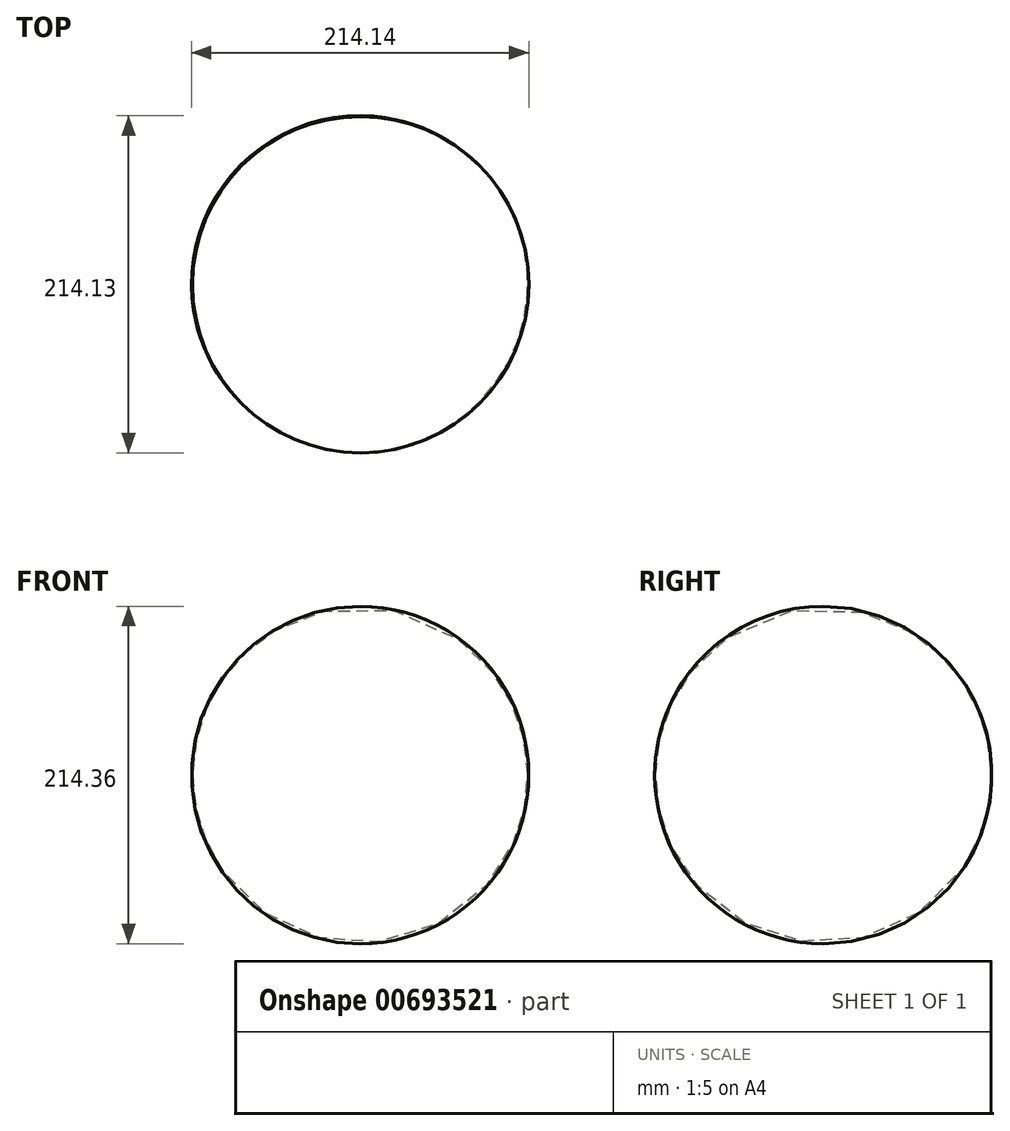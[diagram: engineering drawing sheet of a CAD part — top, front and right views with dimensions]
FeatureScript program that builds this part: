
annotation { "Feature Type Name" : "Feature", "Feature Type Description" : "" }
export const myFeature = defineFeature(function(context is Context, id is Id, definition is map)
    precondition{}
    {
        {
            var Q0;
            Q0=qCreatedBy(makeId("Top.planeOp"),FACE);
            var sketch = newSketch(context, id + "F0", { "sketchPlane" : qUnion([Q0])});
            skArc(sketch, "E0", {"start": v(76.82, 76.54) * mm, "mid": v(-74.48, 76.5) * mm, "end": v(-73.9, -74.8) * mm});
            skLineSegment(sketch, "E1", {"start": v(-73.9, -74.8) * mm, "end": v(76.82, 76.54) * mm});
            skSolve(sketch);
        }
        {
            var Q0;
            Q0=makeQuery(id+"F0.imprint","IMPRINT",FACE,{"disambiguationData":[TD([[makeQuery(id+"F0.imprint","IMPRINT",EDGE,{"derivedFrom":sQuery(id+"F0.wireOp",EDGE,"E0")}),1.0]])]});
            var Q1;
            Q1=sQuery(id+"F0.wireOp",EDGE,"E1");
            revolve(context, id + "F1", {"entities" : qUnion([Q0]), "axis" : qUnion([Q1]), "revolveType" : RevolveType.FULL});
        }
    });
